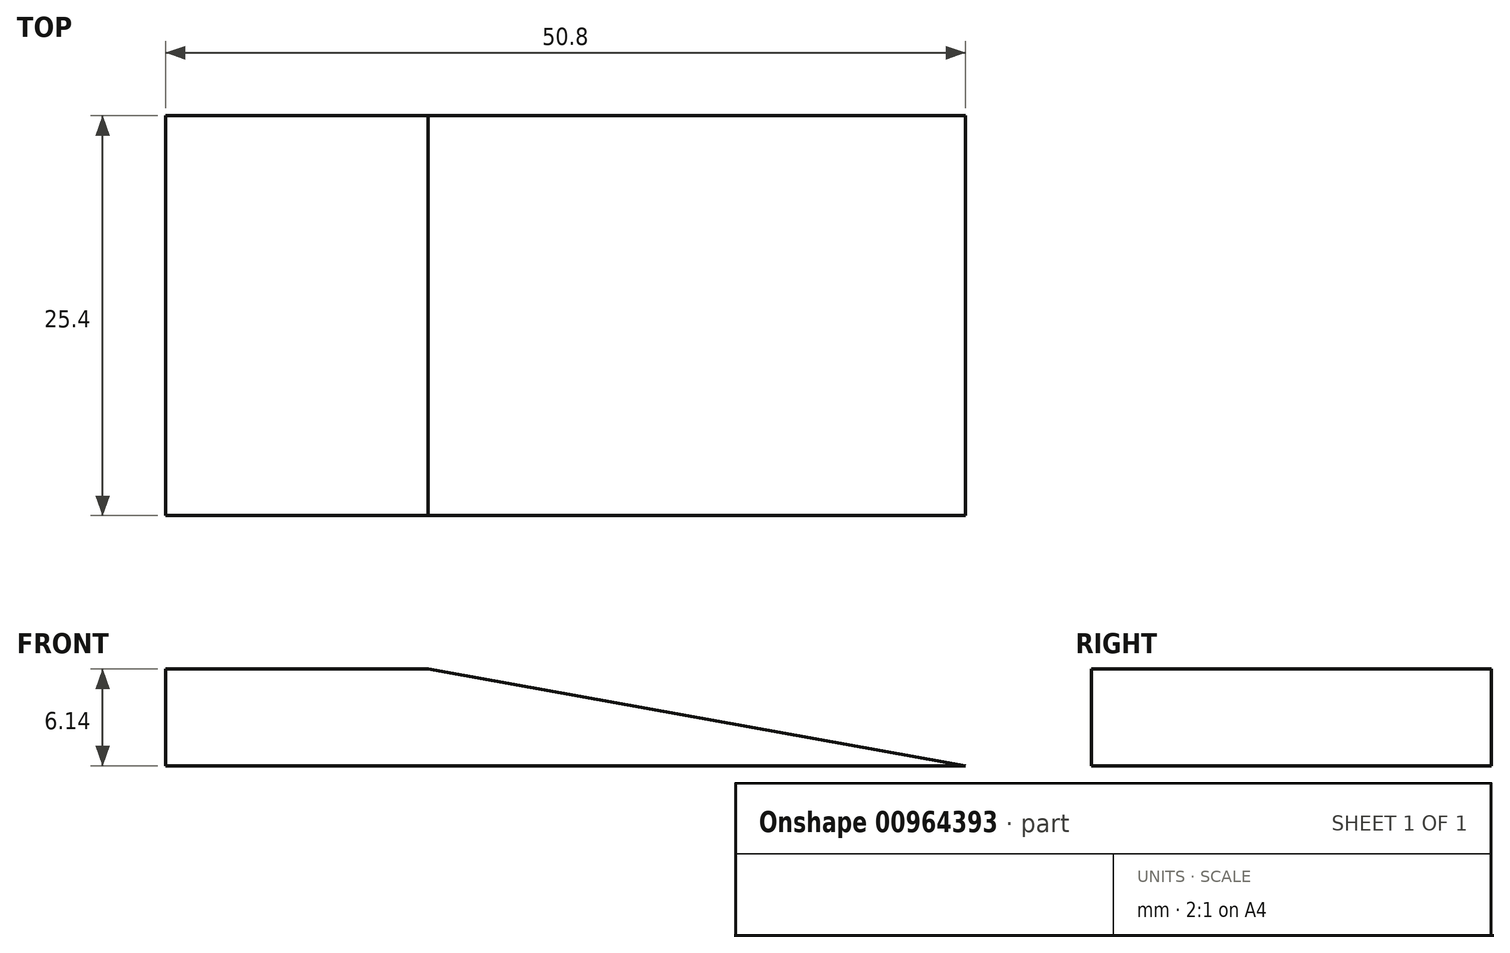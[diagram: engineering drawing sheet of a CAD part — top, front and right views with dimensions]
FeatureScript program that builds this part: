
annotation { "Feature Type Name" : "Feature", "Feature Type Description" : "" }
export const myFeature = defineFeature(function(context is Context, id is Id, definition is map)
    precondition{}
    {
        {
            var Q0;
            Q0=qCreatedBy(makeId("Front.planeOp"),FACE);
            var sketch = newSketch(context, id + "F0", { "sketchPlane" : qUnion([Q0])});
            skLineSegment(sketch, "E0", {"start": v(0, 0) * mm, "end": v(50.8, 0) * mm});
            skLineSegment(sketch, "E1", {"start": v(50.8, 0) * mm, "end": v(16.67, 6.14) * mm});
            skLineSegment(sketch, "E2", {"start": v(16.67, 6.14) * mm, "end": v(0, 6.14) * mm});
            skLineSegment(sketch, "E3", {"start": v(0, 6.14) * mm, "end": v(0, 0) * mm});
            skSolve(sketch);
        }
        {
            var Q0;
            Q0 = qSketchRegion(id + "F0", true);
            extrude(context, id + "F1", {"entities" : qUnion([Q0]), "depth" : 25.4 * mm, "offsetDistance" : 25.4 * mm});
        }
    });
